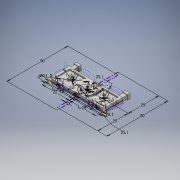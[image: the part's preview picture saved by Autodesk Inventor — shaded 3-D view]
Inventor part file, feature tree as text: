
AUTODESK INVENTOR PART (.ipt)
format: ipt  version: 2016 (Build 200138000, 138)  size: 353,280 bytes
history: native  units: mm
features: extrude x8, other x3, sketch x3, hole x2, fillet x2
ambient origin geometry x8: Origin, YZ Plane, XZ Plane, XY Plane, X Axis, Y Axis, Z Axis, Center Point
bodies: Body1 (feature_tree)
feature tree (18):
  other  "構築線"
  extrude  "押し出し11"  Depth=17.0mm
  extrude  "押し出し12"  Depth=5.6mm
  extrude  "押し出し13"  Depth=10.0mm
  extrude  "押し出し16"  Depth=25.0mm
  other  "固定穴"
  extrude  "押し出し19"  Depth=8.6mm
  extrude  "押し出し20"  TaperAngle=0.0deg  [1 undecoded]
  extrude  "押し出し21"  Depth=20.1mm
  other  "ねじ穴+固定(基板)"
  hole  "ねじ穴(基板)"  [1 undecoded]
  extrude  "押し出し22"  Depth=25.0mm
  fillet  "フィレット1"  Radius=3.0mm
  fillet  "フィレット2"  Radius=20.1mm
  hole  "穴4"  [1 undecoded]
  sketch  "スケッチ8"
  sketch  "スケッチ9"
  sketch  "スケッチ12"
note: 3 required parameter values undecoded (feature->parameter linkage not recoverable at this tier; creation-order binding heuristic only, values carry confidence <= 0.55)
